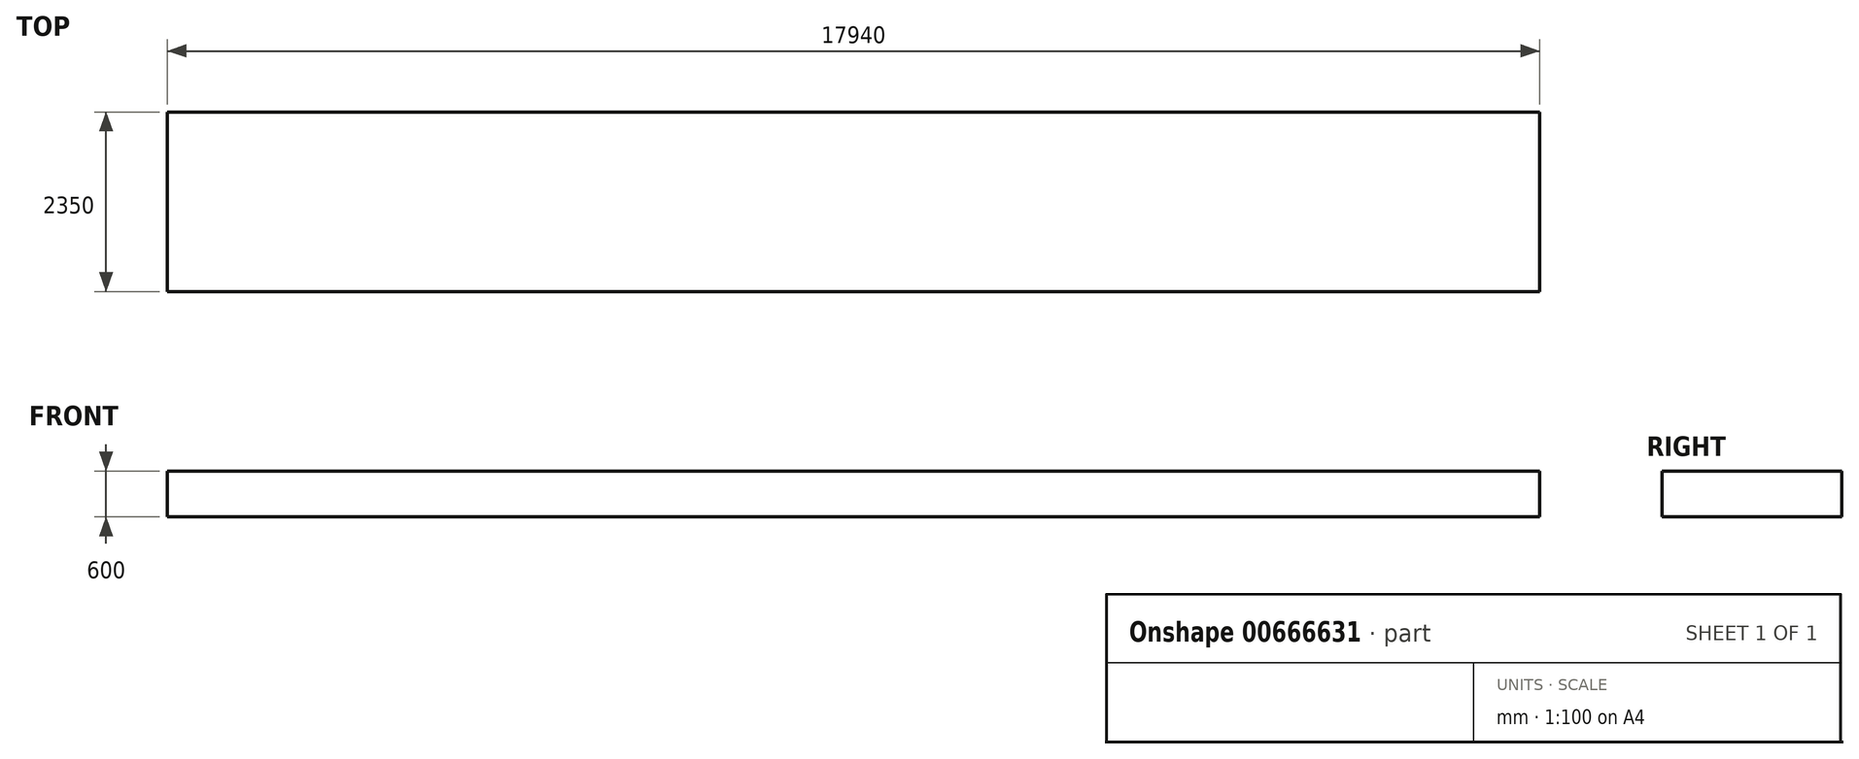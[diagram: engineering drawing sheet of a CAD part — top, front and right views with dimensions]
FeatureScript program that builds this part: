
annotation { "Feature Type Name" : "Feature", "Feature Type Description" : "" }
export const myFeature = defineFeature(function(context is Context, id is Id, definition is map)
    precondition{}
    {
        {
            var Q0;
            Q0=qCreatedBy(makeId("Top.planeOp"),FACE);
            var sketch = newSketch(context, id + "F0", { "sketchPlane" : qUnion([Q0])});
            skLineSegment(sketch, "E0.bottom", {"start": v(-18276.95, 2346.28) * mm, "end": v(-336.95, 2346.28) * mm});
            skLineSegment(sketch, "E0.top", {"start": v(-18276.95, -3.72) * mm, "end": v(-336.95, -3.72) * mm});
            skLineSegment(sketch, "E0.left", {"start": v(-18276.95, 2346.28) * mm, "end": v(-18276.95, -3.72) * mm});
            skLineSegment(sketch, "E0.right", {"start": v(-336.95, 2346.28) * mm, "end": v(-336.95, -3.72) * mm});
            skSolve(sketch);
        }
        {
            var Q0;
            Q0=makeQuery(id+"F0.imprint","IMPRINT",FACE,{"disambiguationData":[TD([[makeQuery(id+"F0.imprint","IMPRINT",EDGE,{"derivedFrom":sQuery(id+"F0.wireOp",EDGE,"E0.bottom")}),-1.0]])]});
            extrude(context, id + "F1", {"entities" : qUnion([Q0]), "depth" : 600 * mm, "offsetDistance" : 25 * mm});
        }
    });
